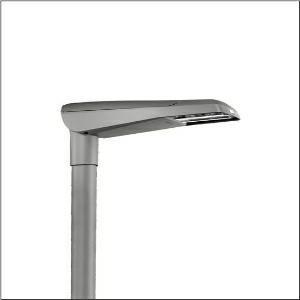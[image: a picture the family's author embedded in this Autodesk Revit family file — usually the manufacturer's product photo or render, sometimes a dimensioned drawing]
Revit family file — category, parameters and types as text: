
# Revit family: streetlight_sl_11_iq_micro___st1_0ab_5xc1n51f08ce_cbf6
name_source: partatom
category: Lighting Fixtures
units: mm (PartAtom-declared; Revit-internal decimal feet)

## family parameters
Cut with Voids When Loaded = No
Host = Face
Light Source = No
Part Type = Normal
Room Calculation Point = No
Round Connector Dimension = Use Diameter
Shared = No

## types (1)
- --- (1 x LED, 1580 lm, 12.6 W, 3000K)
    Apparent Load = 13 VA
    CIE Flux Codes = 29 63 95 100 100
    Color Rendering = 70
    Color Temperature = 3000K
    Default Elevation = 1800 mm
    Description = Streetlight SL 11 iQ micro, mast luminaire, primary light control with 3 zone facetted reflector, of plastic, silver coated, highly specular, primary optical cover: cover, of PMMA, transparent, light distribution: ST1.0aB, light emission: direct distribution, primary light characteristic: asymmetric, installation type: post-top, side-entry, lamps: LED, High Power LED, rated values: 1.580lm | 12,6W | 125,4lm/W (begin service life); end service life: 1.580lm | 12,9W; at 50% lumin. flux: 790lm | 6,8W | 116,2lm/W, colour temperature: 3000K, colour rendering: CRI > 70, light colour: 730, light setting 1 begin service life: 100% | 1.580lm | 12,6W | 125,4lm/W | 3.000K, light setting 1 end service life: 12,9W, further light settings possible, control: optimised constant luminous flux control (CLO 2.0), Desk-Remote (wireless, voltage-free reading and setting of iQ features in the workshop via application-optimized NFC function/RFID function), Light-Fading, Smart-Wire, Night-Set, Lumen-Switch, Temp-Guard, Auto-Match, Street-Remote, with cable H07RN-F 3x 1.5mm², mains connection: 230..240V, AC, 50/60Hz, connection cable pre-assembled, cable length: 5,5m, luminaire housing, of diecast aluminium, powder-coated, SITECO metallic grey (DB 702S), please order mast flange separately, inclination adjustable without tools: 0°, 5°, 10°, 15° (post-top) | 0°, -5°, -10°, -15° (side-entry), sealing non-destructively replaceable, multi-level sealing system, length: 600mm, width: 174mm, height: 116mm, mast flange for spigot size: 42mm (side-entry): 5XC10008XM4, 60/48mm (side-entry/post-top): 5XC10108XM2, 76/60mm (side-entry/post-top): 5XC10108XM1, equipment: standard, protection rating (complete): IP66, insulation class (complete): insulation class II (safety insulation), certification: CE, ENEC, ENEC+, VDE, impact resistance: IK10, permissible operating ambient temperature for outdoor applications: -25..+50°C, standard-compliant lighting for roads and squares, Environmental Product Declaration (EPD) tested and certified by an independent institute, packaging unit: 1 piece

Light Distribution: ST1.0aB
    Height = 116 mm
    Lamp = 1 x LED
    Lamp Light Flux = 1580 lm
    Lamp Power = 12.6 W
    Lamp count = 1
    Length = 600 mm
    Luminous efficacy = 125 lm/W
    Manufacturer = Siteco
    ModVariant = No
    Model = 5XC1N51F08CE
    Number of Poles = 1
    OnlyDefault = Yes
    Power Factor = 1
    Product Name = Streetlight SL 11 iQ micro | ST1.0aB
    Product group = mast luminaire | pylon top
    ProductGroupID = 6100
    Protection Class = Protection class II
    Protection Degree = IP 66
    RLX_Detail_Level = 1
    RLX_Emergency_Light_Flux = 0 lm
    RLX_Emergency_Type = 0
    RLX_Emergency_Type_DB = No
    RlxData = <blob elided: 26273 chars, md5=42ab956e>
    Socket = socket
    Standby Power = 0 W
    System Light Flux = 1580 lm
    System Power = 13 W
    Type Comments = factory setting: luminous flux: 100 % | dim-lin: 254 | 229 mA
    Type Image = l_1006566.jpg
    URL = http://relux.com
    VarID = @adj_020891
    Voltage = 0 V
    Weight = 0.00 kg
    Width = 174 mm

## geometry (parser evidence)
native form markers: Blend x4, Sweep x11
no freeform markers — native parametric forms only
